# Revit family: HB_Firescreen_Temperature_T
name_source: partatom
category: Doors
units: mm (PartAtom-declared; Revit-internal decimal feet)

## family parameters
Always vertical = Yes
Cut with Voids When Loaded = No
Host = Wall
OmniClass Number = 23.30.10.21.11.11
OmniClass Title = Rolling Fire Doors
Room Calculation Point = No
Shared = No

## types (2) — shared parameters
Clear_height = 3000 mm  [stored 9.84252 ft]
Clear_height_maximum = 4000 mm  [stored 13.1234 ft]
Clear_height_minimum = 1000 mm  [stored 3.28084 ft]
Clear_width = 4000 mm  [stored 13.1234 ft]
Clear_width_maximum = 5000 mm  [stored 16.4042 ft]
Clear_width_minimum = 1000 mm  [stored 3.28084 ft]
Construction Type = Inside mount and on the wall
Description = Firescreen® Temperture T1 / T2 - EI₁30-EI₂30 / EI₁60-EI₂60
Dimension_override = Product size OK
Fire Resistance = Tested according to standard EN 13501-2. Fire resistance classes EI130, EI230,
EI160 and EI260.
FireExit = No
Function = Interior
Guid_rail_material = HB_Sendzimir galvanised sheet steel
HandicapAccessible = Yes
Headbox_height = 310 mm  [stored 1.01706 ft]
Headbox_height_calc = 310 mm  [stored 1.01706 ft]
Headbox_material = HB_Sendzimir galvanised sheet steel
Headbox_width = 455 mm
Headbox_width_calc = 455 mm
Height = 3000 mm  [stored 9.84252 ft]
IfcDoorTypeOperationEnum = ROLLINGUP
Installation_space_height = 100 mm  [stored 0.328084 ft]
Installation_space_length = 350 mm  [stored 1.14829 ft]
IsExternal = No
LoadBearing = No
Manufacturer = Hoefnagels Fire Safety
Operation = ROLLINGUP
Product_datasheet_URL = https://www.hoefnagels.com
Product_dimension_daylight_is_valid = Yes
Rough Height = 3000 mm  [stored 9.84252 ft]
Rough Width = 4000 mm  [stored 13.1234 ft]
Screen_material = HB_double-walled technical textile, filled with intumescent material Provided
with a silicone-based, smoke-proof grey coating
SelfClosing = Yes
Side_guide_rail_depth = 80 mm  [stored 0.262467 ft]
Side_guide_rail_width = 213 mm  [stored 0.698819 ft]
SmokeStop = Yes
Thickness = 455 mm
Wall Closure = By host
Warning_sign = No
Width = 4000 mm  [stored 13.1234 ft]
zero-valued in all types: Filling_belt_thickness

## per-type parameters (varying)
| type | Fire Rating | FireRating | Model |
| HB_Firescreen_Temperature_T1_30min | EI1 30/ EI2 30 | 30 | Fire-resistant roller curtain, Firescreen® T1 - EI₁30/EI₂30 |
| HB_Firescreen_Temperature_T2_60min | EI1 60/ EI2 60 | 60 | Fire-resistant roller curtain, Firescreen ® T2 - EI₁60/EI₂60 |

note: [stored X ft] marks values corroborated as IEEE doubles in the binary element streams (Revit-internal decimal feet)

## geometry (parser evidence)
native form markers: Sweep x5
no freeform markers — native parametric forms only
